# Revit family: rba-bim-B8236
name_source: partatom
category: Specialty Equipment
revit_build: Autodesk Revit 2018 (Build: 20170223_1515(x64)
units: mm (PartAtom-declared; Revit-internal decimal feet)

## family parameters
Always vertical = Yes
Cut with Voids When Loaded = No
OmniClass Number = 23.40.20.21.34
OmniClass Title = Soap Holders, Dispensers
Part Type = Normal
Room Calculation Point = No
Round Connector Dimension = Use Diameter
Shared = Yes
Work Plane-Based = Yes

## types (1)
- B-8236
    ADA Compliant = Yes
    Assembly Code = C1030210
    Default Elevation = 0 mm  [stored 0 ft]
    Description = Bobrick Top-Fill Counter-Mounted Manual Foam Soap Dispenser
    Height = 153.99 mm
    Installation Type = Counter-Mounted
    Length = 152.4 mm  [stored 0.5 ft]
    Manufacturer = Bobrick Washroom Equipment, Inc
    Materials and Finishes = Stainless Steel Polished
    Model = B8236
    Modified Issue = 20220412.01
    Price = Prices may vary. Please consult Manufacturer Representative for most up-to-date price list.
    Product Page URL = http://www.bobrick.com
    Specification = Top-fill counter-mounted manual foam soap dispenser shall dispense 7ml of foam using 0.5ml of commercially marketed foam soaps. Cover shall be constructed of durable die-cast zinc with bright polish finish. Spout assembly shall be type-304 stainless steel with bright polished finish. Dispenser shall be equipped with integrated funnel to facilitate re-filling of soap. Spout shall rotate 360° without damage to valve mechanism. Valve shall be operable with one hand and with less than 5 pounds of force (22.2 N) to comply with accessible design (including ADAAG in U.S.A.). Escutcheon shall lock to body with concealed locking mechanism that is opened with special key provided. Foam Dispensing assembly shall be removable from top for filling and maintenance. Shank shall accommodate mounting thicknesses up to 3'' (76mm). Translucent, shatter-resistant polyethylene container shall have a capacity of 34-fl oz (1.0-L).
    URL = http://www.bobrick.com
    Warranty Information = 3 Year Limited Warranty
    Width = 65.09 mm

note: [stored X ft] marks values corroborated as IEEE doubles in the binary element streams (Revit-internal decimal feet)

## geometry (parser evidence)
native form markers: Sweep x2
no freeform markers — native parametric forms only
